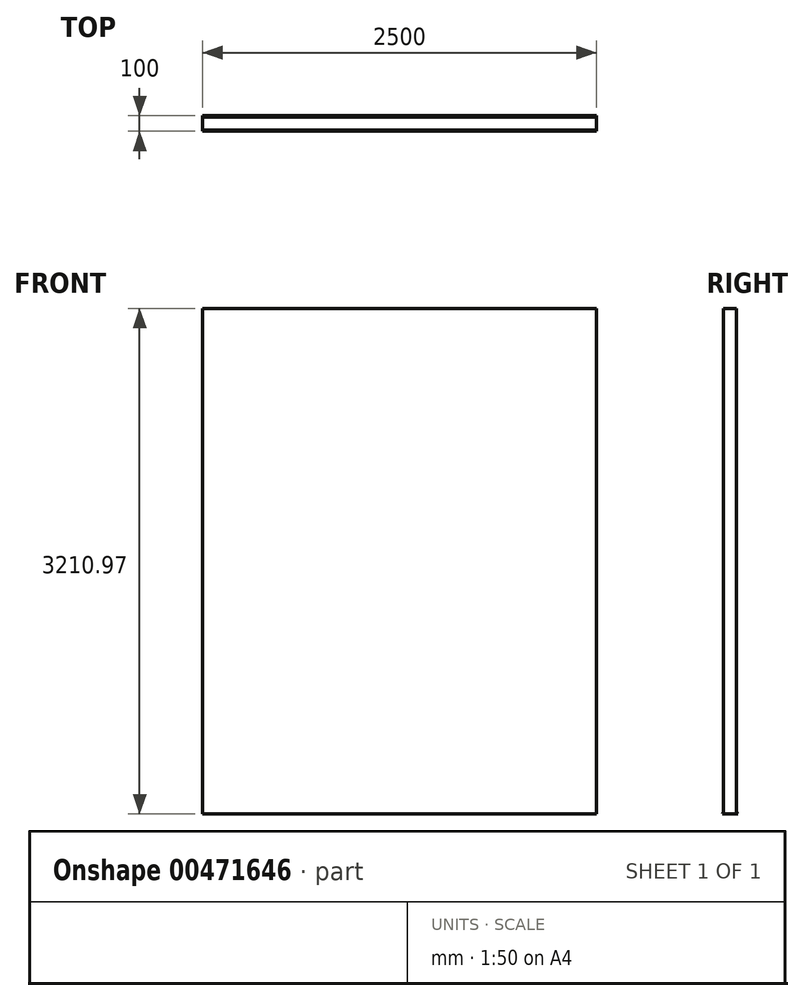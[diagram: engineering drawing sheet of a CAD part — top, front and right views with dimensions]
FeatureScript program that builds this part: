
annotation { "Feature Type Name" : "Feature", "Feature Type Description" : "" }
export const myFeature = defineFeature(function(context is Context, id is Id, definition is map)
    precondition{}
    {
        {
            var Q0;
            Q0=qCreatedBy(makeId("Right.planeOp"),FACE);
            var sketch = newSketch(context, id + "F0", { "sketchPlane" : qUnion([Q0])});
            skLineSegment(sketch, "E0", {"start": v(0, 0) * mm, "end": v(50, 0) * mm});
            skLineSegment(sketch, "E1", {"start": v(50, 0) * mm, "end": v(44.25, 8) * mm});
            skLineSegment(sketch, "E2", {"start": v(41.44, 16.75) * mm, "end": v(41.44, 100.97) * mm});
            skLineSegment(sketch, "E3", {"start": v(41.44, 100.97) * mm, "end": v(0, 100.97) * mm});
            skLineSegment(sketch, "E4", {"start": v(0, 100.97) * mm, "end": v(0, 0) * mm});
            skLineSegment(sketch, "E5.MirrorCS", {"start": v(-41.44, 100.97) * mm, "end": v(0, 100.97) * mm});
            skLineSegment(sketch, "E6.MirrorCS", {"start": v(0, 0) * mm, "end": v(-50, 0) * mm});
            skLineSegment(sketch, "E7.MirrorCS", {"start": v(-50, 0) * mm, "end": v(-44.25, 8) * mm});
            skLineSegment(sketch, "E8.MirrorCS", {"start": v(-41.44, 16.75) * mm, "end": v(-41.44, 100.97) * mm});
            skPoint(sketch, "E9.visualSharp", {"position": v(41.44, 11.92) * mm});
            skArc(sketch, "E9.filletArc", {"start": v(41.44, 16.75) * mm, "mid": v(42.16, 12.16) * mm, "end": v(44.25, 8) * mm});
            skPoint(sketch, "E10.visualSharp", {"position": v(-41.44, 11.92) * mm});
            skArc(sketch, "E10.filletArc", {"start": v(-44.25, 8) * mm, "mid": v(-42.16, 12.16) * mm, "end": v(-41.44, 16.75) * mm});
            skSolve(sketch);
        }
        {
            var Q0;
            Q0=makeQuery(id+"F0.imprint","IMPRINT",FACE,{"disambiguationData":[TD([[makeQuery(id+"F0.imprint","IMPRINT",EDGE,{"derivedFrom":sQuery(id+"F0.wireOp",EDGE,"E4")}),-1.0]])]});
            var Q1;
            Q1=makeQuery(id+"F0.imprint","IMPRINT",FACE,{"disambiguationData":[TD([[makeQuery(id+"F0.imprint","IMPRINT",EDGE,{"derivedFrom":sQuery(id+"F0.wireOp",EDGE,"E0")}),1.0]])]});
            extrude(context, id + "F1", {"entities" : qUnion([Q0, Q1]), "depth" : 2500 * mm});
        }
        {
            var Q0;
            Q0=makeQuery(id+"F1.opExtrude","SWEPT_FACE",FACE,{"disambiguationData":[OSD([sQuery(id+"F0.wireOp",EDGE,"E3"),sQuery(id+"F0.wireOp",EDGE,"E5.MirrorCS")])]});
            extrude(context, id + "F2", {"entities" : qUnion([Q0]), "operationType" : NewBodyOperationType.ADD, "depth" : 3110 * mm});
        }
    });
